# Revit family: QF_COZIL_FFCP-70N
name_source: partatom
category: Equipamento especial
units: mm (PartAtom-declared; Revit-internal decimal feet)

## family parameters
Com base no plano de trabalho = Não
Compartilhado = Não
Corte com vazios quando carregada = Não
Cota do conector redondo = Utilizar diâmetro
Número OmniClass = 23.40.40.14.17.11
Ponto de cálculo do ambiente = Não
Sempre na vertical = Sim
Tipo de parte = Normal
Título OmniClass = Cookers, Ovens, Stoves

## types (1)
- FFCP-70
    Descrição = FOGAO FRANCES MODULAR A GAS - 700X743X335MM (COMPACT LINE II)
    Elevação padrão = 0  [stored 0 ft]
    Fabricante = COZIL
    Gas Consumption GLP = 0.356 Kg/h
    Gas Consumption GN = 0.4 m³/h
    Gas Input GLP = 16258 Btu/h
    Gas Input GN = 4100 kcal/h
    Gas Pressure GLP = 0.0 bar
    Gas Pressure GN = 0.0 bar
    Gas Size = 1/2"
    Modelo = FFCP-70
    Tray of Waste = 9 L
    URL = https://cozil.com.br

note: [stored X ft] marks values corroborated as IEEE doubles in the binary element streams (Revit-internal decimal feet)
